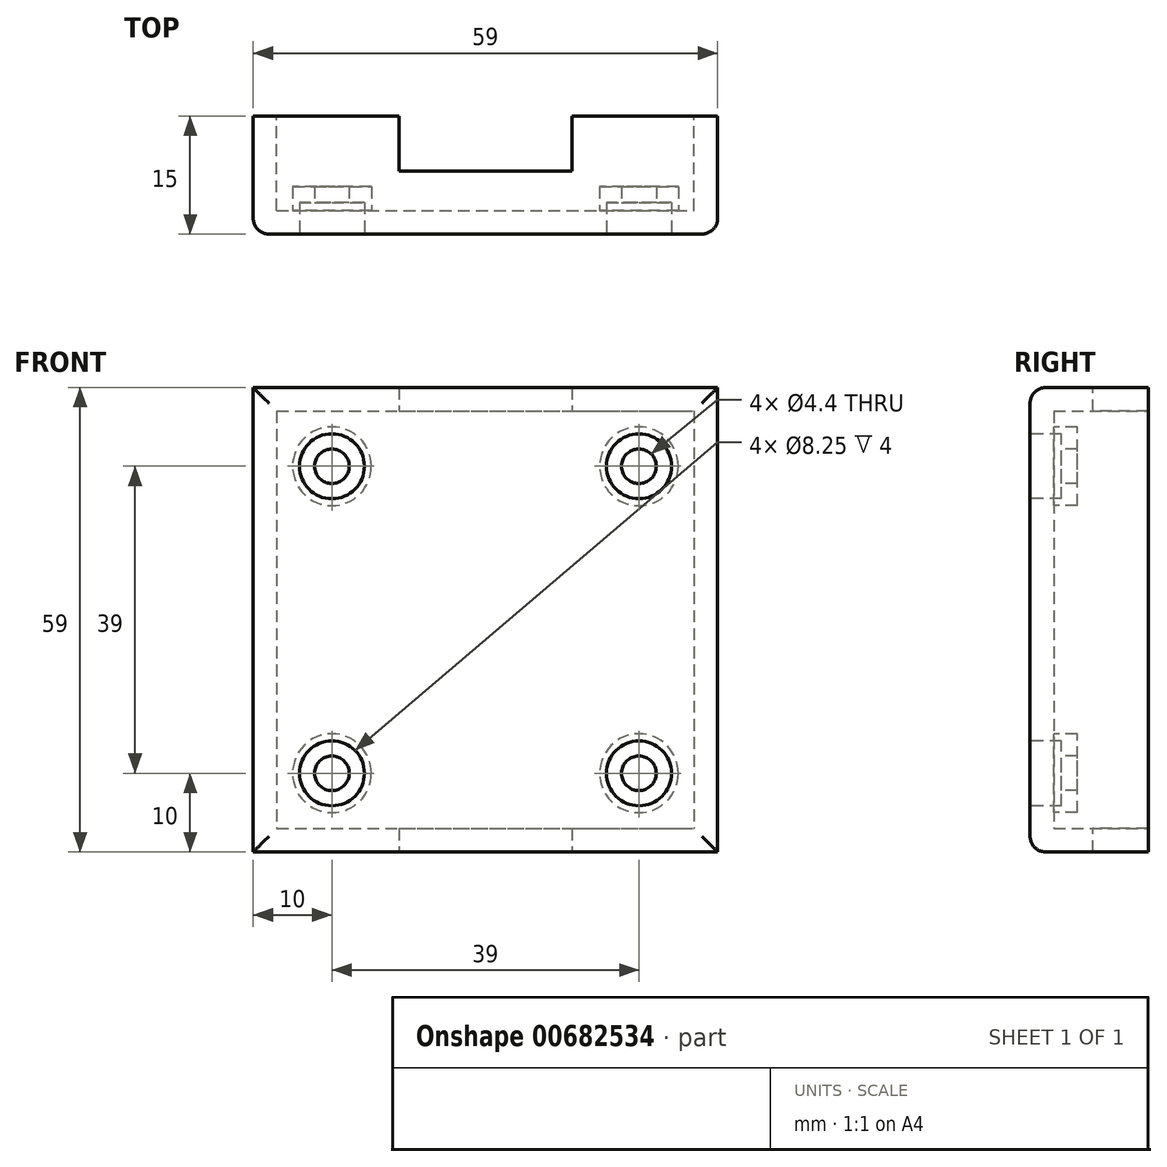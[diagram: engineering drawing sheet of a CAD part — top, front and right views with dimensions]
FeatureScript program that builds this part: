
annotation { "Feature Type Name" : "Feature", "Feature Type Description" : "" }
export const myFeature = defineFeature(function(context is Context, id is Id, definition is map)
    precondition{}
    {
        {
            var Q0;
            Q0=qCreatedBy(makeId("Front.planeOp"),FACE);
            var sketch = newSketch(context, id + "F0", { "sketchPlane" : qUnion([Q0])});
            skLineSegment(sketch, "E0.bottom", {"start": v(-29.5, 29.5) * mm, "end": v(29.5, 29.5) * mm});
            skLineSegment(sketch, "E0.top", {"start": v(-29.5, -29.5) * mm, "end": v(29.5, -29.5) * mm});
            skLineSegment(sketch, "E0.left", {"start": v(-29.5, 29.5) * mm, "end": v(-29.5, -29.5) * mm});
            skLineSegment(sketch, "E0.right", {"start": v(29.5, 29.5) * mm, "end": v(29.5, -29.5) * mm});
            skSolve(sketch);
        }
        {
            var Q0;
            Q0=qCreatedBy(makeId("Front.planeOp"),FACE);
            var sketch = newSketch(context, id + "F1", { "sketchPlane" : qUnion([Q0])});
            skLineSegment(sketch, "E1.bottom", {"start": v(-26.5, 26.5) * mm, "end": v(26.5, 26.5) * mm});
            skLineSegment(sketch, "E1.top", {"start": v(-26.5, -26.5) * mm, "end": v(26.5, -26.5) * mm});
            skLineSegment(sketch, "E1.left", {"start": v(-26.5, 26.5) * mm, "end": v(-26.5, -26.5) * mm});
            skLineSegment(sketch, "E1.right", {"start": v(26.5, 26.5) * mm, "end": v(26.5, -26.5) * mm});
            skSolve(sketch);
        }
        {
            var Q0;
            Q0=qCreatedBy(makeId("Top.planeOp"),FACE);
            var sketch = newSketch(context, id + "F2", { "sketchPlane" : qUnion([Q0])});
            skLineSegment(sketch, "E2.bottom", {"start": v(-11, 7) * mm, "end": v(11, 7) * mm});
            skLineSegment(sketch, "E2.top", {"start": v(-11, -7) * mm, "end": v(11, -7) * mm});
            skLineSegment(sketch, "E2.left", {"start": v(-11, 7) * mm, "end": v(-11, -7) * mm});
            skLineSegment(sketch, "E2.right", {"start": v(11, 7) * mm, "end": v(11, -7) * mm});
            skSolve(sketch);
        }
        {
            var Q0;
            Q0 = qSketchRegion(id + "F0", true);
            extrude(context, id + "F3", {"entities" : qUnion([Q0]), "depth" : 15 * mm, "offsetDistance" : 25 * mm});
        }
        {
            var Q0;
            Q0 = qSketchRegion(id + "F1", true);
            extrude(context, id + "F4", {"entities" : qUnion([Q0]), "operationType" : NewBodyOperationType.REMOVE, "depth" : 12 * mm, "offsetDistance" : 25 * mm});
        }
        {
            var Q0;
            Q0=makeQuery(id+"F2.imprint","IMPRINT",FACE,{"disambiguationData":[TD([[makeQuery(id+"F2.imprint","IMPRINT",EDGE,{"derivedFrom":sQuery(id+"F2.wireOp",EDGE,"E2.bottom")}),-1.0]])]});
            extrude(context, id + "F5", {"entities" : qUnion([Q0]), "operationType" : NewBodyOperationType.REMOVE, "oppositeDirection" : true, "depth" : 30 * mm, "offsetDistance" : 25 * mm, "hasSecondDirection" : true, "secondDirectionOppositeDirection" : false, "secondDirectionDepth" : 30 * mm});
        }
        {
            var Q0;
            Q0=makeQuery(id+"F3.opExtrude","CAP_FACE",FACE,{"disambiguationData":[OSD([sQuery(id+"F0.wireOp",EDGE,"E0.bottom"),sQuery(id+"F0.wireOp",EDGE,"E0.top"),sQuery(id+"F0.wireOp",EDGE,"E0.left"),sQuery(id+"F0.wireOp",EDGE,"E0.right")])],"isStart":false});
            fillet(context, id + "F6", {"entities" : qUnion([Q0]), "radius" : 2 * mm, "tangentPropagation" : true, "allowEdgeOverflow" : false});
        }
        {
            var Q0;
            Q0=qCreatedBy(makeId("Front.planeOp"),FACE);
            cPlane(context, id + "F7", {"entities" : qUnion([Q0]), "cplaneType" : CPlaneType.OFFSET, "offset" : 15 * mm, "width" : 150 * mm, "height" : 150 * mm});
        }
        {
            var Q0;
            Q0=qCreatedBy(id+"F7.planeOp",FACE);
            var sketch = newSketch(context, id + "F8", { "sketchPlane" : qUnion([Q0])});
            skCircle(sketch, "E3", {"center": v(19.5, 19.5) * mm, "radius": 5 * mm});
            skCircle(sketch, "E4.MirrorC", {"center": v(-19.5, 19.5) * mm, "radius": 5 * mm});
            skCircle(sketch, "E5.MirrorC", {"center": v(19.5, -19.5) * mm, "radius": 5 * mm});
            skCircle(sketch, "E6.MirrorC", {"center": v(-19.5, -19.5) * mm, "radius": 5 * mm});
            skSolve(sketch);
        }
        {
            var Q0;
            Q0 = qSketchRegion(id + "F8", true);
            extrude(context, id + "F9", {"entities" : qUnion([Q0]), "operationType" : NewBodyOperationType.ADD, "oppositeDirection" : true, "depth" : 6 * mm, "offsetDistance" : 25 * mm});
        }
        {
            var Q0;
            Q0=qCreatedBy(id+"F7.planeOp",FACE);
            var sketch = newSketch(context, id + "F10", { "sketchPlane" : qUnion([Q0])});
            skPoint(sketch, "E7", {"position": v(-19.5, 19.5) * mm});
            skPoint(sketch, "E8", {"position": v(19.5, 19.5) * mm});
            skPoint(sketch, "E9", {"position": v(19.5, -19.5) * mm});
            skPoint(sketch, "E10", {"position": v(-19.5, -19.5) * mm});
            skSolve(sketch);
        }
        {
            var Q0;
            Q0=sQuery(id+"F10.wireOp",VERTEX,"E7");
            var Q1;
            Q1=makeQuery(id+"F3.opExtrude","SWEPT_BODY",BODY,{"disambiguationData":[OSD([sQuery(id+"F0.wireOp",EDGE,"E0.bottom"),sQuery(id+"F0.wireOp",EDGE,"E0.top"),sQuery(id+"F0.wireOp",EDGE,"E0.left"),sQuery(id+"F0.wireOp",EDGE,"E0.right")])]});
            hole(context, id + "F11", {"style" : HoleStyle.C_BORE, "endStyle" : HoleEndStyle.THROUGH, "standardTappedOrClearance" : lookupTablePath({ "standard" : "ISO", "fit" : "Normal", "size" : "M4", "type" : "Clearance" }), "standardBlindInLast" : lookupTablePath({ "fit" : "Standard", "standard" : "ISO", "size" : "M4", "type" : "Clearance" }), "holeDiameter" : 4.4 * mm, "cBoreDiameter" : 8.25 * mm, "cBoreDepth" : 4 * mm, "majorDiameter" : 5 * mm, "isTappedThrough" : true, "tappedDepth" : 12 * mm, "tapClearance" : 3, "locations" : qUnion([Q0]), "scope" : qUnion([Q1])});
        }
        {
            var Q0;
            Q0=sQuery(id+"F10.wireOp",VERTEX,"E10");
            var Q1;
            Q1=makeQuery(id+"F3.opExtrude","SWEPT_BODY",BODY,{"disambiguationData":[OSD([sQuery(id+"F0.wireOp",EDGE,"E0.bottom"),sQuery(id+"F0.wireOp",EDGE,"E0.top"),sQuery(id+"F0.wireOp",EDGE,"E0.left"),sQuery(id+"F0.wireOp",EDGE,"E0.right")])]});
            hole(context, id + "F12", {"style" : HoleStyle.C_BORE, "endStyle" : HoleEndStyle.THROUGH, "standardTappedOrClearance" : lookupTablePath({ "standard" : "ISO", "fit" : "Normal", "size" : "M4", "type" : "Clearance" }), "standardBlindInLast" : lookupTablePath({ "fit" : "Standard", "standard" : "ISO", "size" : "M4", "type" : "Clearance" }), "holeDiameter" : 4.4 * mm, "cBoreDiameter" : 8.25 * mm, "cBoreDepth" : 4 * mm, "majorDiameter" : 5 * mm, "isTappedThrough" : true, "tappedDepth" : 12 * mm, "tapClearance" : 3, "locations" : qUnion([Q0]), "scope" : qUnion([Q1])});
        }
        {
            var Q0;
            Q0=sQuery(id+"F10.wireOp",VERTEX,"E9");
            var Q1;
            Q1=makeQuery(id+"F3.opExtrude","SWEPT_BODY",BODY,{"disambiguationData":[OSD([sQuery(id+"F0.wireOp",EDGE,"E0.bottom"),sQuery(id+"F0.wireOp",EDGE,"E0.top"),sQuery(id+"F0.wireOp",EDGE,"E0.left"),sQuery(id+"F0.wireOp",EDGE,"E0.right")])]});
            hole(context, id + "F13", {"style" : HoleStyle.C_BORE, "endStyle" : HoleEndStyle.THROUGH, "standardTappedOrClearance" : lookupTablePath({ "standard" : "ISO", "fit" : "Normal", "size" : "M4", "type" : "Clearance" }), "standardBlindInLast" : lookupTablePath({ "fit" : "Standard", "standard" : "ISO", "size" : "M4", "type" : "Clearance" }), "holeDiameter" : 4.4 * mm, "cBoreDiameter" : 8.25 * mm, "cBoreDepth" : 4 * mm, "majorDiameter" : 5 * mm, "isTappedThrough" : true, "tappedDepth" : 12 * mm, "tapClearance" : 3, "locations" : qUnion([Q0]), "scope" : qUnion([Q1])});
        }
        {
            var Q0;
            Q0=sQuery(id+"F10.wireOp",VERTEX,"E8");
            var Q1;
            Q1=makeQuery(id+"F3.opExtrude","SWEPT_BODY",BODY,{"disambiguationData":[OSD([sQuery(id+"F0.wireOp",EDGE,"E0.bottom"),sQuery(id+"F0.wireOp",EDGE,"E0.top"),sQuery(id+"F0.wireOp",EDGE,"E0.left"),sQuery(id+"F0.wireOp",EDGE,"E0.right")])]});
            hole(context, id + "F14", {"style" : HoleStyle.C_BORE, "endStyle" : HoleEndStyle.THROUGH, "standardTappedOrClearance" : lookupTablePath({ "standard" : "ISO", "fit" : "Normal", "size" : "M4", "type" : "Clearance" }), "standardBlindInLast" : lookupTablePath({ "fit" : "Standard", "standard" : "ISO", "size" : "M4", "type" : "Clearance" }), "holeDiameter" : 4.4 * mm, "cBoreDiameter" : 8.25 * mm, "cBoreDepth" : 4 * mm, "majorDiameter" : 5 * mm, "isTappedThrough" : true, "tappedDepth" : 12 * mm, "tapClearance" : 3, "locations" : qUnion([Q0]), "scope" : qUnion([Q1])});
        }
    });
